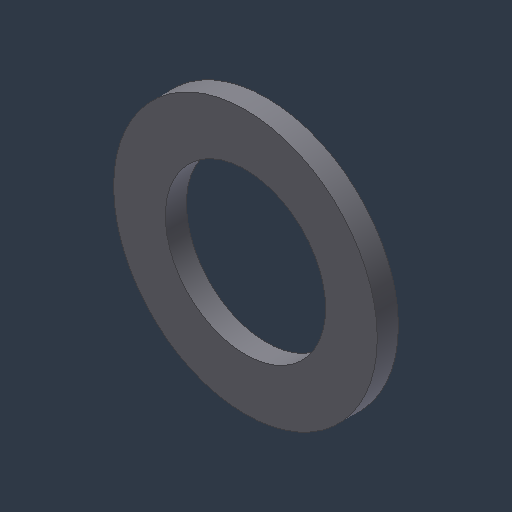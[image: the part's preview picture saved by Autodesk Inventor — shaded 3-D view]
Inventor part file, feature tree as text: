
AUTODESK INVENTOR PART (.ipt)
format: ipt  version: 2024.3 (Build 283343000, 343)  size: 88,064 bytes
history: native  units: mm (DEFAULTED — no unit token found)
features: extrude x1, sketch x1
ambient origin geometry x8: Origin, YZ Plane, XZ Plane, XY Plane, X Axis, Y Axis, Z Axis, Center Point
bodies: Solid1 (feature_tree)
feature tree (2):
  extrude  "Extrusion1"  Depth=1.27mm
  sketch  "Sketch2"  dims[d0=9.652mm d1=15.875mm d2=1.27mm d3=0.0mm d4=0.0mm]
